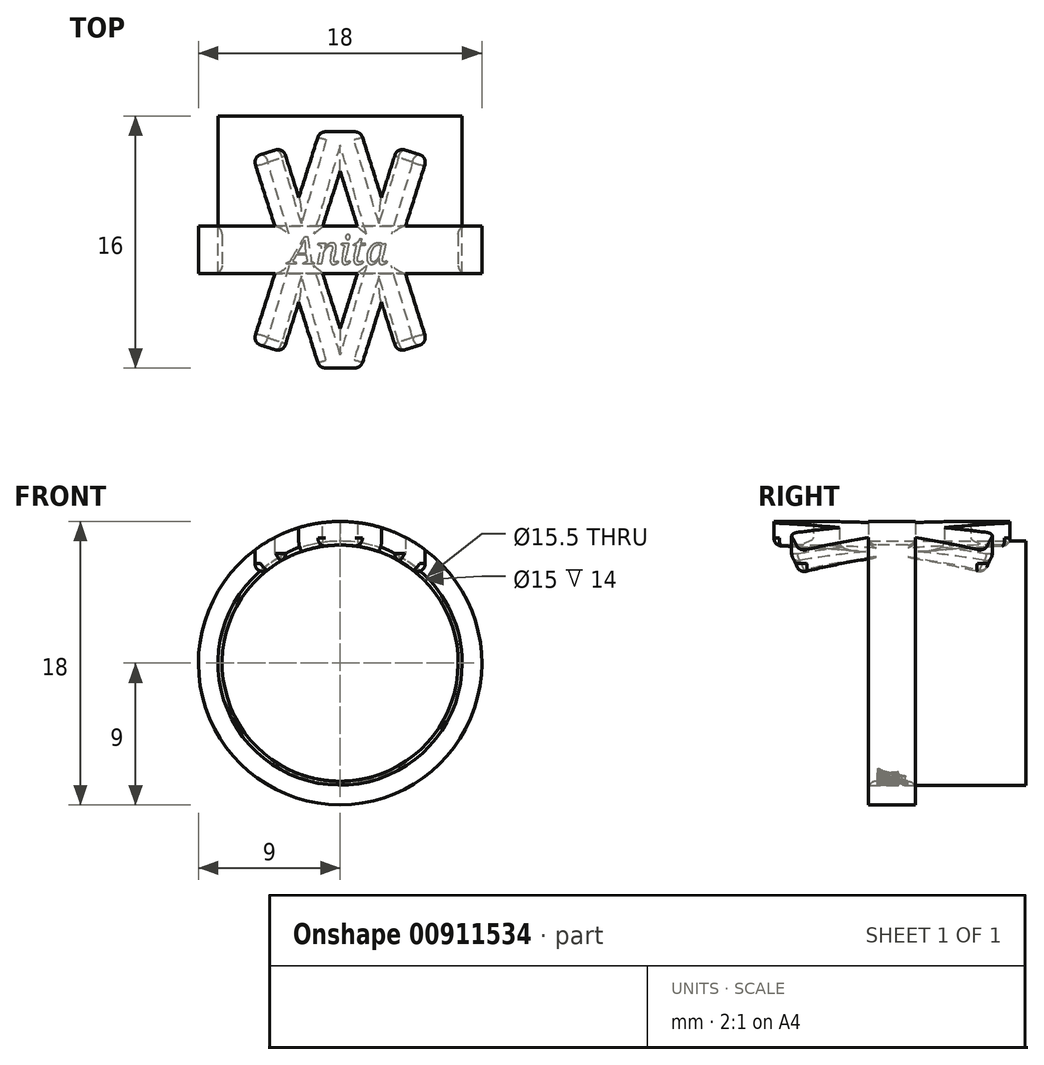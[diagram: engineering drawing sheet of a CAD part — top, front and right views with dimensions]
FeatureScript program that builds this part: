
annotation { "Feature Type Name" : "Feature", "Feature Type Description" : "" }
export const myFeature = defineFeature(function(context is Context, id is Id, definition is map)
    precondition{}
    {
        {
            var Q0;
            Q0=qCreatedBy(makeId("Right.planeOp"),FACE);
            var sketch = newSketch(context, id + "F0", { "sketchPlane" : qUnion([Q0])});
            skLineSegment(sketch, "E0.bottom", {"start": v(-1.5, 9) * mm, "end": v(1.5, 9) * mm});
            skLineSegment(sketch, "E0.top", {"start": v(-1.5, 7.5) * mm, "end": v(1.5, 7.5) * mm});
            skLineSegment(sketch, "E0.left", {"start": v(-1.5, 9) * mm, "end": v(-1.5, 7.5) * mm});
            skLineSegment(sketch, "E0.right", {"start": v(1.5, 9) * mm, "end": v(1.5, 7.5) * mm});
            skLineSegment(sketch, "E1", {"start": v(0, 0) * mm, "end": v(0, 30.06) * mm, "construction": true});
            skLineSegment(sketch, "E2", {"start": v(-13.24, 0) * mm, "end": v(16.31, 0) * mm, "construction": true});
            skSolve(sketch);
        }
        {
            var Q0;
            Q0=makeQuery(id+"F0.imprint","IMPRINT",FACE,{"disambiguationData":[TD([[makeQuery(id+"F0.imprint","IMPRINT",EDGE,{"derivedFrom":sQuery(id+"F0.wireOp",EDGE,"E0.bottom")}),-1.0]])]});
            var Q1;
            Q1=sQuery(id+"F0.wireOp",EDGE,"E2");
            revolve(context, id + "F1", {"entities" : qUnion([Q0]), "axis" : qUnion([Q1]), "revolveType" : RevolveType.FULL});
        }
        {
            var Q0;
            Q0=qCreatedBy(makeId("Top.planeOp"),FACE);
            var sketch = newSketch(context, id + "F2", { "sketchPlane" : qUnion([Q0])});
            skLineSegment(sketch, "E3", {"start": v(0, 6.73) * mm, "end": v(0, -7.13) * mm, "construction": true});
            skLineSegment(sketch, "E4", {"start": v(-3.63, -6.5) * mm, "end": v(0, 5) * mm});
            skLineSegment(sketch, "E5", {"start": v(0, 5) * mm, "end": v(3.63, -6.5) * mm});
            skLineSegment(sketch, "E6", {"start": v(-3.63, -6.5) * mm, "end": v(-5.53, -5.9) * mm});
            skLineSegment(sketch, "E7", {"start": v(-5.53, -5.9) * mm, "end": v(-1.3, 7.5) * mm});
            skLineSegment(sketch, "E8", {"start": v(-1.3, 7.5) * mm, "end": v(1.3, 7.5) * mm});
            skLineSegment(sketch, "E9", {"start": v(1.3, 7.5) * mm, "end": v(5.53, -5.9) * mm});
            skLineSegment(sketch, "E10", {"start": v(3.63, -6.5) * mm, "end": v(5.53, -5.9) * mm});
            skLineSegment(sketch, "E11", {"start": v(-10.55, 0) * mm, "end": v(12.02, 0) * mm, "construction": true});
            skLineSegment(sketch, "E12.MirrorCS", {"start": v(3.63, 6.5) * mm, "end": v(5.53, 5.9) * mm});
            skLineSegment(sketch, "E13.MirrorCS", {"start": v(-3.63, 6.5) * mm, "end": v(-5.53, 5.9) * mm});
            skLineSegment(sketch, "E14.MirrorCS", {"start": v(-5.53, 5.9) * mm, "end": v(-1.3, -7.5) * mm});
            skLineSegment(sketch, "E15.MirrorCS", {"start": v(-3.63, 6.5) * mm, "end": v(0, -5) * mm});
            skLineSegment(sketch, "E16.MirrorCS", {"start": v(0, -5) * mm, "end": v(3.63, 6.5) * mm});
            skLineSegment(sketch, "E17.MirrorCS", {"start": v(-1.3, -7.5) * mm, "end": v(1.3, -7.5) * mm});
            skLineSegment(sketch, "E18.MirrorCS", {"start": v(1.3, -7.5) * mm, "end": v(5.53, 5.9) * mm});
            skSolve(sketch);
        }
        {
            var Q0;
            Q0=makeQuery(id+"F1.opRevolve","SWEPT_FACE",FACE,{"disambiguationData":[OSD([sQuery(id+"F0.wireOp",EDGE,"E0.left")])]});
            var sketch = newSketch(context, id + "F3", { "sketchPlane" : qUnion([Q0])});
            skCircle(sketch, "E19.0", {"center": v(0, 0) * mm, "radius": 7.5 * mm});
            skCircle(sketch, "E20.0", {"center": v(0, 0) * mm, "radius": 9 * mm});
            skSolve(sketch);
        }
        {
            var Q0;
            {var subQ3=sQuery(id+"F2.wireOp",EDGE,"E13.MirrorCS");Q0=makeQuery(id+"F2.imprint","IMPRINT",FACE,{"disambiguationData":[TD([[makeQuery(id+"F2.imprint","IMPRINT",EDGE,{"derivedFrom":subQ3}),1.0]])]});}
            var Q1;
            {var subQ1=sQuery(id+"F2.wireOp",EDGE,"E4");var subQ5=sQuery(id+"F2.wireOp",EDGE,"E14.MirrorCS");var subQ7=makeQuery(id+"F2.imprint","INTERSECT",VERTEX,{"derivedFrom":[subQ1,subQ5]});Q1=makeQuery(id+"F2.imprint","IMPRINT",FACE,{"disambiguationData":[TD([[makeQuery(id+"F2.imprint","IMPRINT",EDGE,{"disambiguationData":[TD([[subQ7,-1.0]])],"derivedFrom":subQ1}),1.0]])]});}
            var Q2;
            {var subQ5=sQuery(id+"F2.wireOp",EDGE,"E6");Q2=makeQuery(id+"F2.imprint","IMPRINT",FACE,{"disambiguationData":[TD([[makeQuery(id+"F2.imprint","IMPRINT",EDGE,{"derivedFrom":subQ5}),-1.0]])]});}
            var Q3;
            {var subQ3=sQuery(id+"F2.wireOp",EDGE,"E17.MirrorCS");Q3=makeQuery(id+"F2.imprint","IMPRINT",FACE,{"disambiguationData":[TD([[makeQuery(id+"F2.imprint","IMPRINT",EDGE,{"derivedFrom":subQ3}),1.0]])]});}
            var Q4;
            {var subQ5=sQuery(id+"F2.wireOp",EDGE,"E10");Q4=makeQuery(id+"F2.imprint","IMPRINT",FACE,{"disambiguationData":[TD([[makeQuery(id+"F2.imprint","IMPRINT",EDGE,{"derivedFrom":subQ5}),1.0]])]});}
            var Q5;
            {var subQ3=sQuery(id+"F2.wireOp",EDGE,"E12.MirrorCS");Q5=makeQuery(id+"F2.imprint","IMPRINT",FACE,{"disambiguationData":[TD([[makeQuery(id+"F2.imprint","IMPRINT",EDGE,{"derivedFrom":subQ3}),-1.0]])]});}
            var Q6;
            {var subQ0=sQuery(id+"F2.wireOp",EDGE,"E18.MirrorCS");var subQ3=sQuery(id+"F2.wireOp",EDGE,"E5");var subQ4=makeQuery(id+"F2.imprint","INTERSECT",VERTEX,{"derivedFrom":[subQ3,subQ0]});Q6=makeQuery(id+"F2.imprint","IMPRINT",FACE,{"disambiguationData":[TD([[makeQuery(id+"F2.imprint","IMPRINT",EDGE,{"disambiguationData":[TD([[subQ4,1.0]])],"derivedFrom":subQ3}),1.0]])]});}
            var Q7;
            {var subQ10=sQuery(id+"F2.wireOp",EDGE,"E8");Q7=makeQuery(id+"F2.imprint","IMPRINT",FACE,{"disambiguationData":[TD([[makeQuery(id+"F2.imprint","IMPRINT",EDGE,{"derivedFrom":subQ10}),-1.0]])]});}
            var Q8;
            Q8=makeQuery(id+"F1.opRevolve","SWEPT_FACE",FACE,{"disambiguationData":[OSD([sQuery(id+"F0.wireOp",EDGE,"E0.bottom")])]});
            extrude(context, id + "F4", {"entities" : qUnion([Q0, Q1, Q2, Q3, Q4, Q5, Q6, Q7]), "operationType" : NewBodyOperationType.ADD, "endBound" : BoundingType.UP_TO_SURFACE, "endBoundEntityFace" : qUnion([Q8]), "depth" : 25 * mm});
        }
        {
            var Q0;
            Q0=makeQuery(id+"F3.imprint","IMPRINT",FACE,{"disambiguationData":[TD([[makeQuery(id+"F3.imprint","IMPRINT",EDGE,{"derivedFrom":sQuery(id+"F3.wireOp",EDGE,"E19.0")}),1.0]])]});
            extrude(context, id + "F5", {"entities" : qUnion([Q0]), "operationType" : NewBodyOperationType.REMOVE, "endBound" : BoundingType.SYMMETRIC, "oppositeDirection" : true, "depth" : 25 * mm});
        }
        {
            var Q0;
            Q0=makeQuery(id+"F4.opExtrude","SWEPT_EDGE",EDGE,{"disambiguationData":[OSD([sQuery(id+"F2.wireOp",EDGE,"E12.MirrorCS"),sQuery(id+"F2.wireOp",EDGE,"E18.MirrorCS")])]});
            var Q1;
            Q1=makeQuery(id+"F4.opExtrude","SWEPT_EDGE",EDGE,{"disambiguationData":[OSD([sQuery(id+"F2.wireOp",EDGE,"E12.MirrorCS"),sQuery(id+"F2.wireOp",EDGE,"E16.MirrorCS")])]});
            var Q2;
            Q2=makeQuery(id+"F4.opExtrude","SWEPT_EDGE",EDGE,{"disambiguationData":[OSD([sQuery(id+"F2.wireOp",EDGE,"E8"),sQuery(id+"F2.wireOp",EDGE,"E9")])]});
            var Q3;
            Q3=makeQuery(id+"F4.opExtrude","SWEPT_EDGE",EDGE,{"disambiguationData":[OSD([sQuery(id+"F2.wireOp",EDGE,"E7"),sQuery(id+"F2.wireOp",EDGE,"E8")])]});
            var Q4;
            Q4=makeQuery(id+"F4.opExtrude","SWEPT_EDGE",EDGE,{"disambiguationData":[OSD([sQuery(id+"F2.wireOp",EDGE,"E13.MirrorCS"),sQuery(id+"F2.wireOp",EDGE,"E15.MirrorCS")])]});
            var Q5;
            Q5=makeQuery(id+"F4.opExtrude","SWEPT_EDGE",EDGE,{"disambiguationData":[OSD([sQuery(id+"F2.wireOp",EDGE,"E13.MirrorCS"),sQuery(id+"F2.wireOp",EDGE,"E14.MirrorCS")])]});
            var Q6;
            Q6=makeQuery(id+"F4.opExtrude","SWEPT_EDGE",EDGE,{"disambiguationData":[OSD([sQuery(id+"F2.wireOp",EDGE,"E6"),sQuery(id+"F2.wireOp",EDGE,"E7")])]});
            var Q7;
            Q7=makeQuery(id+"F4.opExtrude","SWEPT_EDGE",EDGE,{"disambiguationData":[OSD([sQuery(id+"F2.wireOp",EDGE,"E4"),sQuery(id+"F2.wireOp",EDGE,"E6")])]});
            var Q8;
            Q8=makeQuery(id+"F4.opExtrude","SWEPT_EDGE",EDGE,{"disambiguationData":[OSD([sQuery(id+"F2.wireOp",EDGE,"E14.MirrorCS"),sQuery(id+"F2.wireOp",EDGE,"E17.MirrorCS")])]});
            var Q9;
            Q9=makeQuery(id+"F4.opExtrude","SWEPT_EDGE",EDGE,{"disambiguationData":[OSD([sQuery(id+"F2.wireOp",EDGE,"E17.MirrorCS"),sQuery(id+"F2.wireOp",EDGE,"E18.MirrorCS")])]});
            var Q10;
            Q10=makeQuery(id+"F4.opExtrude","SWEPT_EDGE",EDGE,{"disambiguationData":[OSD([sQuery(id+"F2.wireOp",EDGE,"E5"),sQuery(id+"F2.wireOp",EDGE,"E10")])]});
            var Q11;
            Q11=makeQuery(id+"F4.opExtrude","SWEPT_EDGE",EDGE,{"disambiguationData":[OSD([sQuery(id+"F2.wireOp",EDGE,"E9"),sQuery(id+"F2.wireOp",EDGE,"E10")])]});
            fillet(context, id + "F6", {"entities" : qUnion([Q0, Q1, Q2, Q3, Q4, Q5, Q6, Q7, Q8, Q9, Q10, Q11]), "radius" : .5 * mm, "tangentPropagation" : true, "allowEdgeOverflow" : false});
        }
        {
            var Q0;
            {var subQ0=makeQuery(id+"F1.opRevolve","SWEPT_FACE",FACE,{"disambiguationData":[OSD([sQuery(id+"F0.wireOp",EDGE,"E0.top")])]});var subQ2=sQuery(id+"F2.wireOp",EDGE,"E5");var subQ6=sQuery(id+"F2.wireOp",EDGE,"E4");var subQ8=makeQuery(id+"F2.imprint","INTERSECT",VERTEX,{"derivedFrom":[subQ6,subQ2]});var subQ15=sQuery(id+"F2.wireOp",EDGE,"E7");Q0=makeQuery(id+"F5.boolean.opBoolean","MERGE",FACE,{"derivedFrom":[makeQuery(id+"F4.boolean.opBoolean","SPLIT",FACE,{"disambiguationData":[TD([makeQuery(id+"F4.opExtrude","SWEPT_FACE",FACE,{"disambiguationData":[OSD([subQ6]),TDD([makeQuery(id+"F2.imprint","IMPRINT",EDGE,{"disambiguationData":[TD([[subQ8,1.0]])],"derivedFrom":subQ6})])]})])],"derivedFrom":subQ0}),makeQuery(id+"F4.boolean.opBoolean","SPLIT",FACE,{"disambiguationData":[TD([makeQuery(id+"F4.opExtrude","SWEPT_FACE",FACE,{"disambiguationData":[OSD([subQ15]),TDD([makeQuery(id+"F2.imprint","IMPRINT",EDGE,{"disambiguationData":[TD([[makeQuery(id+"F2.imprint","INTERSECT",VERTEX,{"derivedFrom":[sQuery(id+"F2.wireOp",EDGE,"E6"),subQ15]}),-1.0]])],"derivedFrom":subQ15})])]})])],"derivedFrom":subQ0}),makeQuery(id+"F5.opExtrude","SWEPT_FACE",FACE,{"disambiguationData":[OSD([sQuery(id+"F3.wireOp",EDGE,"E19.0")])]})]});}
            fillet(context, id + "F7", {"entities" : qUnion([Q0]), "radius" : .5 * mm, "tangentPropagation" : true, "allowEdgeOverflow" : false});
        }
        {
            var Q0;
            Q0=qCreatedBy(makeId("Top.planeOp"),FACE);
            var sketch = newSketch(context, id + "F8", { "sketchPlane" : qUnion([Q0])});
            skText(sketch, "E21", { "text": "Anita", "fontName": "NotoSerif-Italic.ttf"});
            const initialGuessF8  = {"E21": [-0.00327, -0.0009, 1, 0, 0.00177]};
            skSetInitialGuess(sketch, initialGuessF8);
            skSolve(sketch);
        }
        {
            var Q0;
            {var subQ3=sQuery(id+"F2.wireOp",EDGE,"E7");var subQ5=sQuery(id+"F2.wireOp",EDGE,"E6");Q0=makeQuery(id+"F4.boolean.opBoolean","SPLIT",FACE,{"disambiguationData":[TD([makeQuery(id+"F4.opExtrude","SWEPT_FACE",FACE,{"disambiguationData":[OSD([subQ3]),TDD([makeQuery(id+"F2.imprint","IMPRINT",EDGE,{"disambiguationData":[TD([[makeQuery(id+"F2.imprint","INTERSECT",VERTEX,{"derivedFrom":[subQ5,subQ3]}),-1.0]])],"derivedFrom":subQ3})])]})])],"derivedFrom":makeQuery(id+"F1.opRevolve","SWEPT_FACE",FACE,{"disambiguationData":[OSD([sQuery(id+"F0.wireOp",EDGE,"E0.left")])]})});}
            var sketch = newSketch(context, id + "F9", { "sketchPlane" : qUnion([Q0])});
            skCircle(sketch, "E22", {"center": v(0, 0) * mm, "radius": 7.75 * mm});
            skSolve(sketch);
        }
        {
            var Q0;
            {var subQ0=sQuery(id+"F9.wireOp",EDGE,"E22");Q0=makeQuery(id+"F9.imprint","IMPRINT",FACE,{"disambiguationData":[TD([[makeQuery(id+"F9.imprint","IMPRINT",EDGE,{"disambiguationData":[OD(0.0)],"derivedFrom":subQ0}),-1.0]])]});}
            var Q1;
            Q1=sQuery(id+"F9.wireOp",EDGE,"E22");
            extrude(context, id + "F10", {"entities" : qUnion([Q0]), "bodyType" : ToolBodyType.SURFACE, "surfaceEntities" : qUnion([Q1]), "oppositeDirection" : true, "depth" : 10 * mm});
        }
        {
            var Q0;
            Q0=qSketchRegion(id+"F8",true);
            var Q1;
            Q1=makeQuery(id+"F10.opExtrude","SWEPT_FACE",FACE,{"disambiguationData":[OSD([sQuery(id+"F9.wireOp",EDGE,"E22")])]});
            extrude(context, id + "F11", {"entities" : qUnion([Q0]), "operationType" : NewBodyOperationType.REMOVE, "endBound" : BoundingType.UP_TO_SURFACE, "oppositeDirection" : true, "endBoundEntityFace" : qUnion([Q1]), "depth" : 25 * mm});
        }
    });
